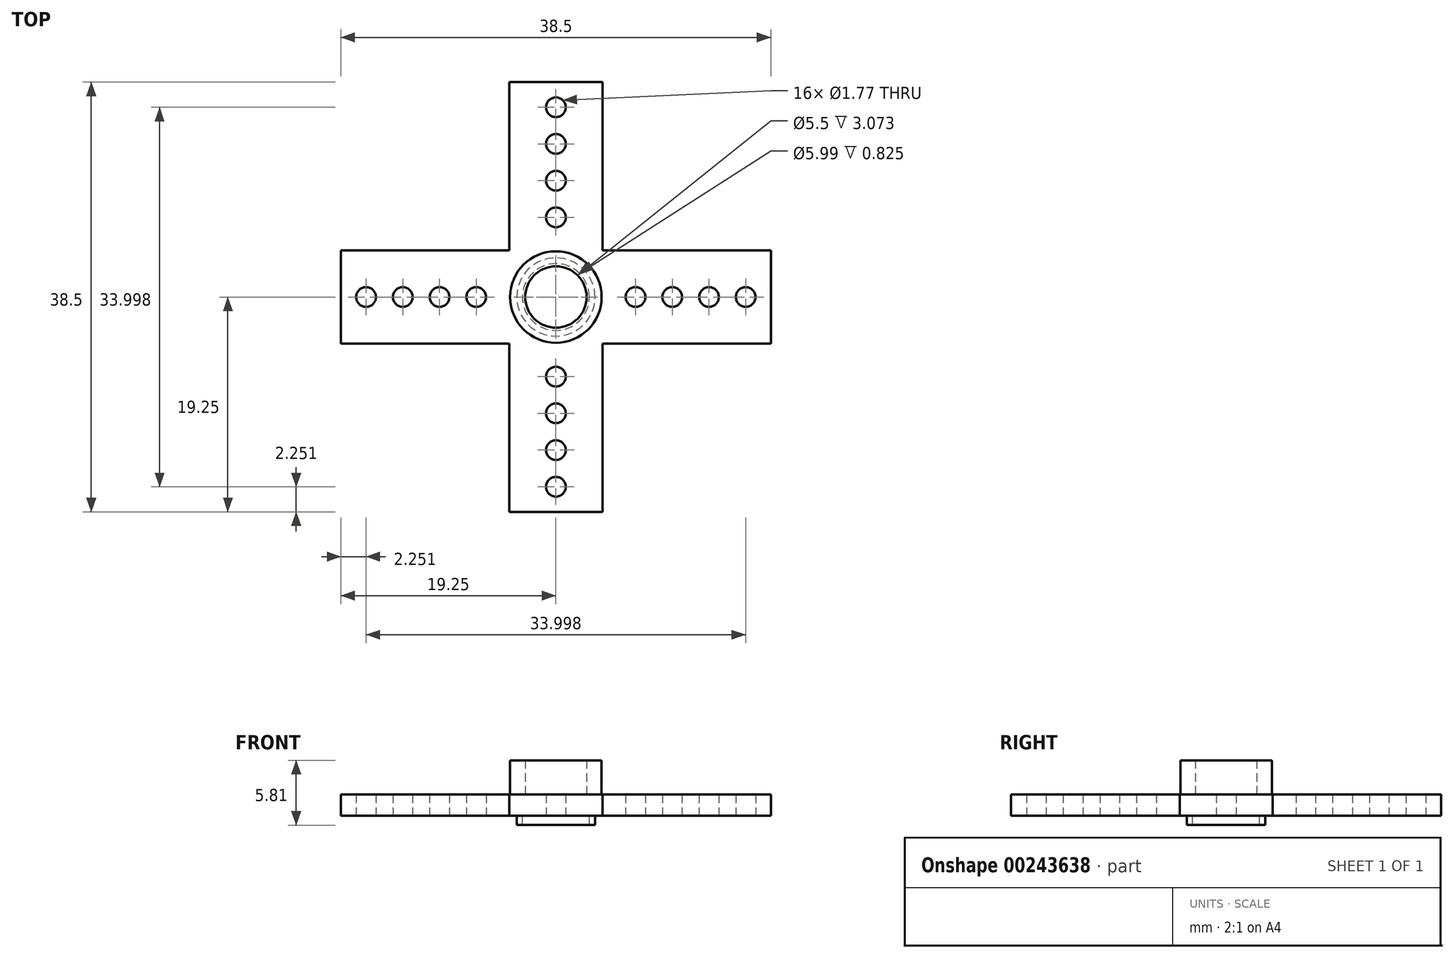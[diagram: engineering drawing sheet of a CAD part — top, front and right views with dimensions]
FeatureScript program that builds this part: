
annotation { "Feature Type Name" : "Feature", "Feature Type Description" : "" }
export const myFeature = defineFeature(function(context is Context, id is Id, definition is map)
    precondition{}
    {
        {
            var Q0;
            Q0=qCreatedBy(makeId("Top.planeOp"),FACE);
            var sketch = newSketch(context, id + "F0", { "sketchPlane" : qUnion([Q0])});
            skLineSegment(sketch, "E0.bottom", {"start": v(4.17, 19.25) * mm, "end": v(-4.17, 19.25) * mm});
            skLineSegment(sketch, "E0.top", {"start": v(4.17, -19.25) * mm, "end": v(-4.17, -19.25) * mm});
            skLineSegment(sketch, "E0.left", {"start": v(4.17, 19.25) * mm, "end": v(4.17, -19.25) * mm});
            skLineSegment(sketch, "E0.right", {"start": v(-4.17, 19.25) * mm, "end": v(-4.17, -19.25) * mm});
            skPoint(sketch, "E0.middle", {"position": v(0, 0) * mm});
            skCircle(sketch, "E1", {"center": v(0, 17) * mm, "radius": 0.88 * mm});
            skCircle(sketch, "E2", {"center": v(0, 13.7) * mm, "radius": 0.88 * mm});
            skCircle(sketch, "E3", {"center": v(0, 10.42) * mm, "radius": 0.88 * mm});
            skCircle(sketch, "E4", {"center": v(0, 7.13) * mm, "radius": 0.88 * mm});
            skCircle(sketch, "E5", {"center": v(0, 0) * mm, "radius": 4.1 * mm});
            skCircle(sketch, "E6", {"center": v(0, 0) * mm, "radius": 2.75 * mm});
            skCircle(sketch, "E7.MirrorC", {"center": v(0, -7.13) * mm, "radius": 0.88 * mm});
            skCircle(sketch, "E8.MirrorC", {"center": v(0, -10.42) * mm, "radius": 0.88 * mm});
            skCircle(sketch, "E9.MirrorC", {"center": v(0, -13.7) * mm, "radius": 0.88 * mm});
            skCircle(sketch, "E10.MirrorC", {"center": v(0, -17) * mm, "radius": 0.88 * mm});
            skLineSegment(sketch, "E11.1.0", {"start": v(-19.25, 4.17) * mm, "end": v(-19.25, -4.17) * mm});
            skLineSegment(sketch, "E11.1.1", {"start": v(-19.25, -4.17) * mm, "end": v(19.25, -4.17) * mm});
            skLineSegment(sketch, "E11.1.2", {"start": v(-19.25, 4.17) * mm, "end": v(19.25, 4.17) * mm});
            skCircle(sketch, "E11.1.3", {"center": v(-17, 0) * mm, "radius": 0.88 * mm});
            skCircle(sketch, "E11.1.4", {"center": v(-13.7, 0) * mm, "radius": 0.88 * mm});
            skCircle(sketch, "E11.1.5", {"center": v(-10.42, 0) * mm, "radius": 0.88 * mm});
            skCircle(sketch, "E11.1.6", {"center": v(-7.13, 0) * mm, "radius": 0.88 * mm});
            skLineSegment(sketch, "E11.2.0", {"start": v(-4.17, -19.25) * mm, "end": v(4.17, -19.25) * mm});
            skLineSegment(sketch, "E11.2.1", {"start": v(4.17, -19.25) * mm, "end": v(4.17, 19.25) * mm});
            skLineSegment(sketch, "E11.2.2", {"start": v(-4.17, -19.25) * mm, "end": v(-4.17, 19.25) * mm});
            skLineSegment(sketch, "E11.3.0", {"start": v(19.25, -4.17) * mm, "end": v(19.25, 4.17) * mm});
            skLineSegment(sketch, "E11.3.1", {"start": v(19.25, 4.17) * mm, "end": v(-19.25, 4.17) * mm});
            skLineSegment(sketch, "E11.3.2", {"start": v(19.25, -4.17) * mm, "end": v(-19.25, -4.17) * mm});
            skCircle(sketch, "E11.3.3", {"center": v(17, 0) * mm, "radius": 0.88 * mm});
            skCircle(sketch, "E11.3.4", {"center": v(13.7, 0) * mm, "radius": 0.88 * mm});
            skCircle(sketch, "E11.3.5", {"center": v(10.42, 0) * mm, "radius": 0.88 * mm});
            skCircle(sketch, "E11.3.6", {"center": v(7.13, 0) * mm, "radius": 0.88 * mm});
            skSolve(sketch);
        }
        {
            var Q0;
            Q0 = qSketchRegion(id + "F0", true);
            var Q1;
            Q1=makeQuery(id+"F0.imprint","IMPRINT",FACE,{"disambiguationData":[TD([[makeQuery(id+"F0.imprint","IMPRINT",EDGE,{"derivedFrom":sQuery(id+"F0.wireOp",EDGE,"E5")}),1.0]])]});
            var Q2;
            Q2=makeQuery(id+"F0.imprint","IMPRINT",FACE,{"disambiguationData":[TD([[makeQuery(id+"F0.imprint","IMPRINT",EDGE,{"derivedFrom":sQuery(id+"F0.wireOp",EDGE,"E6")}),1.0]])]});
            extrude(context, id + "F1", {"entities" : qUnion([Q0, Q1, Q2]), "depth" : 1.9 * mm});
        }
        {
            var Q0;
            Q0=makeQuery(id+"F1.opExtrude","CAP_FACE",FACE,{"disambiguationData":[OSD([sQuery(id+"F0.wireOp",EDGE,"E0.bottom"),sQuery(id+"F0.wireOp",EDGE,"E1"),sQuery(id+"F0.wireOp",EDGE,"E2"),sQuery(id+"F0.wireOp",EDGE,"E3"),sQuery(id+"F0.wireOp",EDGE,"E4"),sQuery(id+"F0.wireOp",EDGE,"E11.1.0"),sQuery(id+"F0.wireOp",EDGE,"E11.1.3"),sQuery(id+"F0.wireOp",EDGE,"E11.1.4"),sQuery(id+"F0.wireOp",EDGE,"E11.1.5"),sQuery(id+"F0.wireOp",EDGE,"E11.1.6"),sQuery(id+"F0.wireOp",EDGE,"E11.2.0"),sQuery(id+"F0.wireOp",EDGE,"E11.2.1"),sQuery(id+"F0.wireOp",EDGE,"E11.2.2"),sQuery(id+"F0.wireOp",EDGE,"E10.MirrorC"),sQuery(id+"F0.wireOp",EDGE,"E9.MirrorC"),sQuery(id+"F0.wireOp",EDGE,"E8.MirrorC"),sQuery(id+"F0.wireOp",EDGE,"E7.MirrorC"),sQuery(id+"F0.wireOp",EDGE,"E11.3.0"),sQuery(id+"F0.wireOp",EDGE,"E11.3.1"),sQuery(id+"F0.wireOp",EDGE,"E11.3.2"),sQuery(id+"F0.wireOp",EDGE,"E11.3.3"),sQuery(id+"F0.wireOp",EDGE,"E11.3.4"),sQuery(id+"F0.wireOp",EDGE,"E11.3.5"),sQuery(id+"F0.wireOp",EDGE,"E11.3.6")])],"isStart":false});
            var sketch = newSketch(context, id + "F2", { "sketchPlane" : qUnion([Q0])});
            skCircle(sketch, "E12.0", {"center": v(0, 0) * mm, "radius": 4.1 * mm});
            skCircle(sketch, "E13.0", {"center": v(0, 0) * mm, "radius": 2.75 * mm});
            skSolve(sketch);
        }
        {
            var Q0;
            Q0 = qSketchRegion(id + "F2", true);
            extrude(context, id + "F3", {"entities" : qUnion([Q0]), "operationType" : NewBodyOperationType.ADD, "depth" : 3.07 * mm});
        }
        {
            var Q0;
            Q0=makeQuery(id+"F0.imprint","IMPRINT",FACE,{"disambiguationData":[TD([[makeQuery(id+"F0.imprint","IMPRINT",EDGE,{"derivedFrom":sQuery(id+"F0.wireOp",EDGE,"E6")}),1.0]])]});
            var sketch = newSketch(context, id + "F4", { "sketchPlane" : qUnion([Q0])});
            skCircle(sketch, "E14", {"center": v(0, 0) * mm, "radius": 3.5 * mm});
            skCircle(sketch, "E15.0", {"center": v(0, 0) * mm, "radius": 3 * mm});
            skSolve(sketch);
        }
        {
            var Q0;
            Q0 = qSketchRegion(id + "F4", true);
            extrude(context, id + "F5", {"entities" : qUnion([Q0]), "operationType" : NewBodyOperationType.ADD, "oppositeDirection" : true, "depth" : 0.83 * mm});
        }
    });
